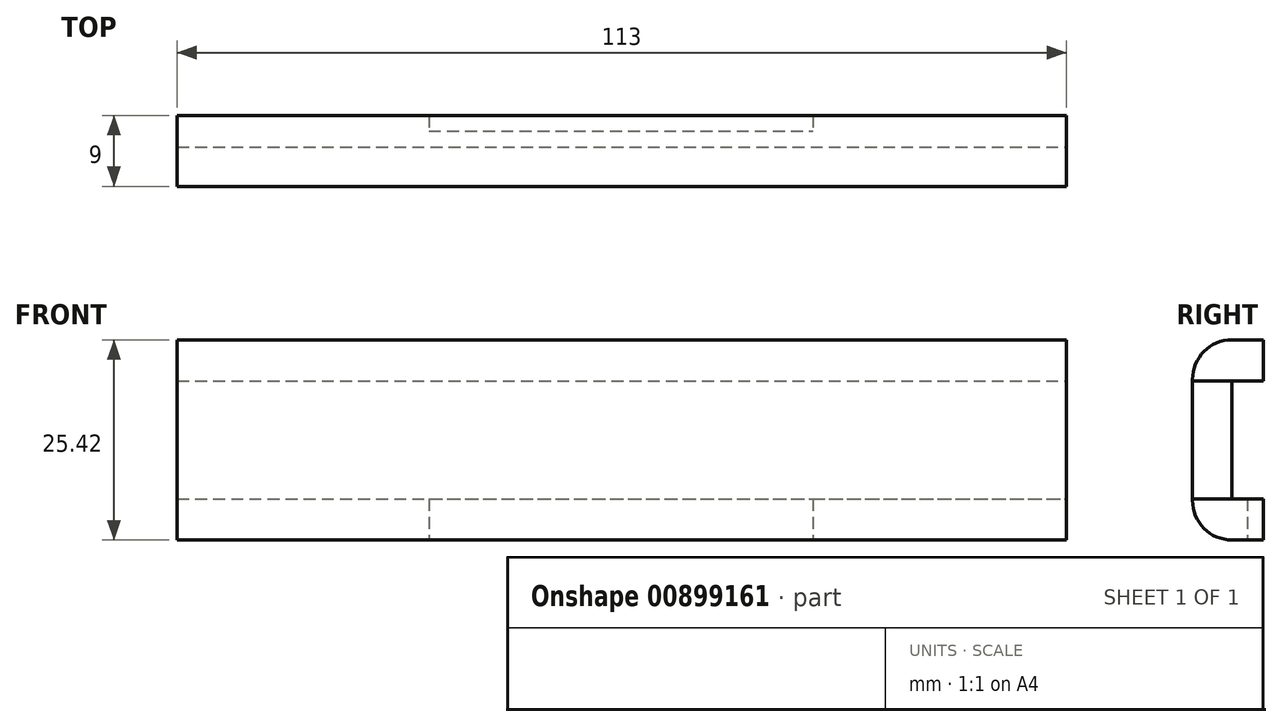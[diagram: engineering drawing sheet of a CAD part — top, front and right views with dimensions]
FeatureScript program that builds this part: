
annotation { "Feature Type Name" : "Feature", "Feature Type Description" : "" }
export const myFeature = defineFeature(function(context is Context, id is Id, definition is map)
    precondition{}
    {
        {
            var Q0;
            Q0=qCreatedBy(makeId("Front.planeOp"),FACE);
            var sketch = newSketch(context, id + "F0", { "sketchPlane" : qUnion([Q0])});
            skLineSegment(sketch, "E0.bottom", {"start": v(-56.5, 7.5) * mm, "end": v(56.5, 7.5) * mm});
            skLineSegment(sketch, "E0.top", {"start": v(-56.5, -7.5) * mm, "end": v(56.5, -7.5) * mm});
            skLineSegment(sketch, "E0.left", {"start": v(-56.5, 7.5) * mm, "end": v(-56.5, -7.5) * mm});
            skLineSegment(sketch, "E0.right", {"start": v(56.5, 7.5) * mm, "end": v(56.5, -7.5) * mm});
            skPoint(sketch, "E0.middle", {"position": v(0, 0) * mm});
            skLineSegment(sketch, "E1.0", {"start": v(-61.5, 12.5) * mm, "end": v(-61.5, -12.5) * mm});
            skLineSegment(sketch, "E1.1", {"start": v(-61.5, 12.5) * mm, "end": v(61.5, 12.5) * mm});
            skLineSegment(sketch, "E1.2", {"start": v(61.5, 12.5) * mm, "end": v(61.5, -12.5) * mm});
            skLineSegment(sketch, "E1.3", {"start": v(-61.5, -12.5) * mm, "end": v(61.5, -12.5) * mm});
            skSolve(sketch);
        }
        {
            var Q0;
            Q0=makeQuery(id+"F0.imprint","IMPRINT",FACE,{"disambiguationData":[TD([[makeQuery(id+"F0.imprint","IMPRINT",EDGE,{"derivedFrom":sQuery(id+"F0.wireOp",EDGE,"E0.bottom")}),-1.0]])]});
            extrude(context, id + "F1", {"entities" : qUnion([Q0]), "oppositeDirection" : true, "depth" : 5 * mm, "offsetDistance" : 25 * mm});
        }
        {
            var Q0;
            Q0=makeQuery(id+"F1.opExtrude","CAP_FACE",FACE,{"disambiguationData":[OSD([sQuery(id+"F0.wireOp",EDGE,"E0.bottom"),sQuery(id+"F0.wireOp",EDGE,"E0.top"),sQuery(id+"F0.wireOp",EDGE,"E0.left"),sQuery(id+"F0.wireOp",EDGE,"E0.right")])],"isStart":true});
            var sketch = newSketch(context, id + "F2", { "sketchPlane" : qUnion([Q0])});
            skLineSegment(sketch, "E2.bottom", {"start": v(56.48, -12.7) * mm, "end": v(-56.48, -12.7) * mm});
            skLineSegment(sketch, "E2.top", {"start": v(56.48, 12.7) * mm, "end": v(-56.48, 12.7) * mm});
            skLineSegment(sketch, "E2.left", {"start": v(56.48, -12.7) * mm, "end": v(56.48, 12.7) * mm});
            skLineSegment(sketch, "E2.right", {"start": v(-56.48, -12.7) * mm, "end": v(-56.48, 12.7) * mm});
            skPoint(sketch, "E2.middle", {"position": v(0, 0) * mm});
            skSolve(sketch);
        }
        {
            var Q0;
            {var subQ0=sQuery(id+"F2.wireOp",EDGE,"E2.top");Q0=makeQuery(id+"F2.imprint","IMPRINT",FACE,{"disambiguationData":[TD([[makeQuery(id+"F2.imprint","IMPRINT",EDGE,{"derivedFrom":subQ0}),1.0]])]});}
            var Q1;
            {var subQ0=sQuery(id+"F2.wireOp",EDGE,"E2.bottom");Q1=makeQuery(id+"F2.imprint","IMPRINT",FACE,{"disambiguationData":[TD([[makeQuery(id+"F2.imprint","IMPRINT",EDGE,{"derivedFrom":subQ0}),-1.0]])]});}
            extrude(context, id + "F3", {"entities" : qUnion([Q0, Q1]), "operationType" : NewBodyOperationType.ADD, "oppositeDirection" : true, "depth" : 9 * mm, "offsetDistance" : 25 * mm});
        }
        {
            var Q0;
            Q0=makeQuery(id+"F3.opExtrude","CAP_EDGE",EDGE,{"disambiguationData":[OSD([sQuery(id+"F2.wireOp",EDGE,"E2.top")])],"isStart":true});
            var Q1;
            Q1=makeQuery(id+"F3.opExtrude","CAP_EDGE",EDGE,{"disambiguationData":[OSD([sQuery(id+"F2.wireOp",EDGE,"E2.bottom")])],"isStart":true});
            fillet(context, id + "F4", {"entities" : qUnion([Q0, Q1]), "radius" : 5 * mm, "tangentPropagation" : true, "allowEdgeOverflow" : false});
        }
        {
            var Q0;
            Q0=makeQuery(id+"F3.opExtrude","SWEPT_FACE",FACE,{"disambiguationData":[OSD([sQuery(id+"F2.wireOp",EDGE,"E2.bottom")])]});
            var sketch = newSketch(context, id + "F5", { "sketchPlane" : qUnion([Q0])});
            skLineSegment(sketch, "E3", {"start": v(-56.48, -9) * mm, "end": v(-24.48, -9) * mm});
            skLineSegment(sketch, "E4", {"start": v(56.48, -7) * mm, "end": v(24.31, -7) * mm});
            skLineSegment(sketch, "E5.bottom", {"start": v(-24.48, -9) * mm, "end": v(24.31, -9) * mm});
            skLineSegment(sketch, "E5.top", {"start": v(-24.48, -7) * mm, "end": v(24.31, -7) * mm});
            skLineSegment(sketch, "E5.left", {"start": v(-24.48, -9) * mm, "end": v(-24.48, -7) * mm});
            skLineSegment(sketch, "E5.right", {"start": v(24.31, -9) * mm, "end": v(24.31, -7) * mm});
            skSolve(sketch);
        }
        {
            var Q0;
            Q0=makeQuery(id+"F5.imprint","IMPRINT",FACE,{"disambiguationData":[TD([[makeQuery(id+"F5.imprint","IMPRINT",EDGE,{"derivedFrom":sQuery(id+"F5.wireOp",EDGE,"E5.bottom")}),-1.0]])]});
            extrude(context, id + "F6", {"entities" : qUnion([Q0]), "operationType" : NewBodyOperationType.REMOVE, "oppositeDirection" : true, "depth" : 10 * mm, "offsetDistance" : 25 * mm});
        }
    });
